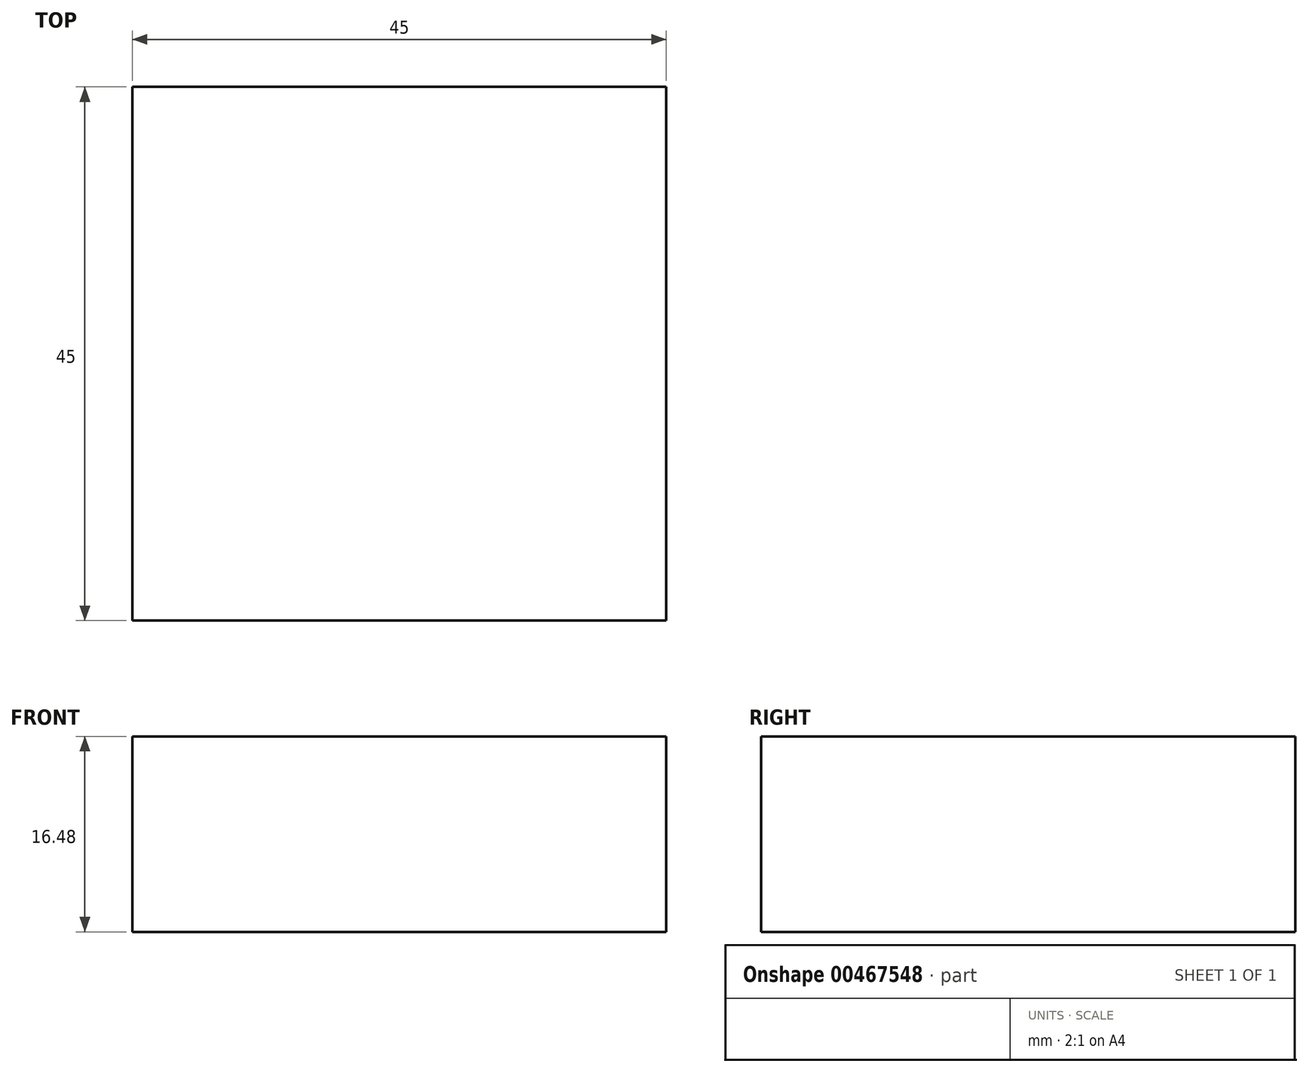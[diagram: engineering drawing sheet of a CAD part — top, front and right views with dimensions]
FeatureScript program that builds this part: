
annotation { "Feature Type Name" : "Feature", "Feature Type Description" : "" }
export const myFeature = defineFeature(function(context is Context, id is Id, definition is map)
    precondition{}
    {
        {
            var Q0;
            Q0=qCreatedBy(makeId("Top.planeOp"),FACE);
            var sketch = newSketch(context, id + "F0", { "sketchPlane" : qUnion([Q0])});
            skLineSegment(sketch, "E0.bottom", {"start": v(0, 0) * mm, "end": v(45, 0) * mm});
            skLineSegment(sketch, "E0.top", {"start": v(0, 45) * mm, "end": v(45, 45) * mm});
            skLineSegment(sketch, "E0.left", {"start": v(0, 0) * mm, "end": v(0, 45) * mm});
            skLineSegment(sketch, "E0.right", {"start": v(45, 0) * mm, "end": v(45, 45) * mm});
            skSolve(sketch);
        }
        {
            var Q0;
            Q0=qSketchRegion(id+"F0",true);
            extrude(context, id + "F1", {"entities" : qUnion([Q0]), "depth" : 8 * 2.06 * mm});
        }
    });
